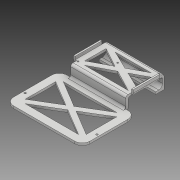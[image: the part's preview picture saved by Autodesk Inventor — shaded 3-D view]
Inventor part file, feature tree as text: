
AUTODESK INVENTOR PART (.ipt)
format: ipt  version: 2018 (Build 220112000, 112)  size: 331,264 bytes
history: native  units: mm
features: extrude x8, sketch x8, fillet x7, other x6
ambient origin geometry x8: Origin, YZ Plane, XZ Plane, XY Plane, X Axis, Y Axis, Z Axis, Center Point
bodies: Body1 (feature_tree)
feature tree (29):
  other  "Sólido1"
  extrude  "Extrusión1"  Depth=70.0mm
  extrude  "Extrusión2"  Depth=22.0mm
  extrude  "Extrusión3"  Depth=2.5mm
  extrude  "Extrusión4"  Depth=10.0mm
  extrude  "Extrusión5"  Depth=10.0mm
  extrude  "Extrusión6"  Depth=5.0mm
  other  "Edición directa1"
  other  "Edición directa2"
  extrude  "Extrusión7"  Depth=5.0mm
  fillet  "Empalme1"  Radius=10.0mm
  fillet  "Empalme2"  Radius=3.0mm
  fillet  "Empalme3"  Radius=15.0mm
  extrude  "Extrusión8"  Depth=3.0mm
  fillet  "Empalme4"  Radius=8.0mm
  fillet  "Empalme5"  Radius=3.0mm
  fillet  "Empalme6"  Radius=12.0mm
  fillet  "Empalme7"  Radius=44.0mm
  sketch  "Boceto1"  dims[d0=100.0mm d1=70.0mm]
  sketch  "Boceto2"  dims[d2=22.0mm d4=22.0mm]
  sketch  "Boceto3"  dims[d6=2.5mm d7=2.5mm]
  sketch  "Boceto4"  dims[d8=10.0mm d9=10.0mm]
  sketch  "Boceto5"  dims[d10=10.0mm d11=10.0mm]
  sketch  "Boceto6"  dims[d12=5.0mm d13=5.0mm]
  sketch  "Boceto7"  dims[d14=5.0mm d15=5.0mm d16=10.0mm d23=3.0mm d24=0.0mm d25=15.0mm]
  sketch  "Boceto8"  dims[d26=50.0mm d27=3.0mm d28=8.0mm d29=3.0mm d30=12.0mm d31=44.0mm d32=3.0mm d33=0.0mm d34=37.0mm d35=37.0mm d36=3.0mm d37=0.0mm d38=17.5mm d39=2.0mm d40=35.0mm d41=2.0mm d42=4.0mm d43=0.0mm d44=3.0mm d45=4.0mm d46=0.0mm d47=35.75mm d48=35.75mm d49=21.5mm d50=21.5mm d52=16.0mm d53=30.0mm d54=2.0mm d55=2.5mm d56=2.5mm d57=2.0mm d58=1.5mm d59=1.5mm d60=2.0mm d61=4.0mm d62=0.0mm d63=0.0mm d64=0.0mm d65=-1.0mm d66=0.0mm d67=0.0mm d68=-2.0mm d69=0.0mm d70=0.0mm d71=0.25mm d72=5.0mm d73=7.5mm d75=10.0mm d77=2.0mm d78=10.0mm d79=2.0mm d80=5.0mm d83=4.0mm d84=0.0mm d85=5.0mm d86=3.0mm d87=3.0mm d88=4.0mm d89=0.0mm d90=10.0mm d91=3.0mm d92=2.0mm d93=3.0mm]
  other  "Desplazar1"
  other  "Desplazar2"
  other  "Desplazar3"
